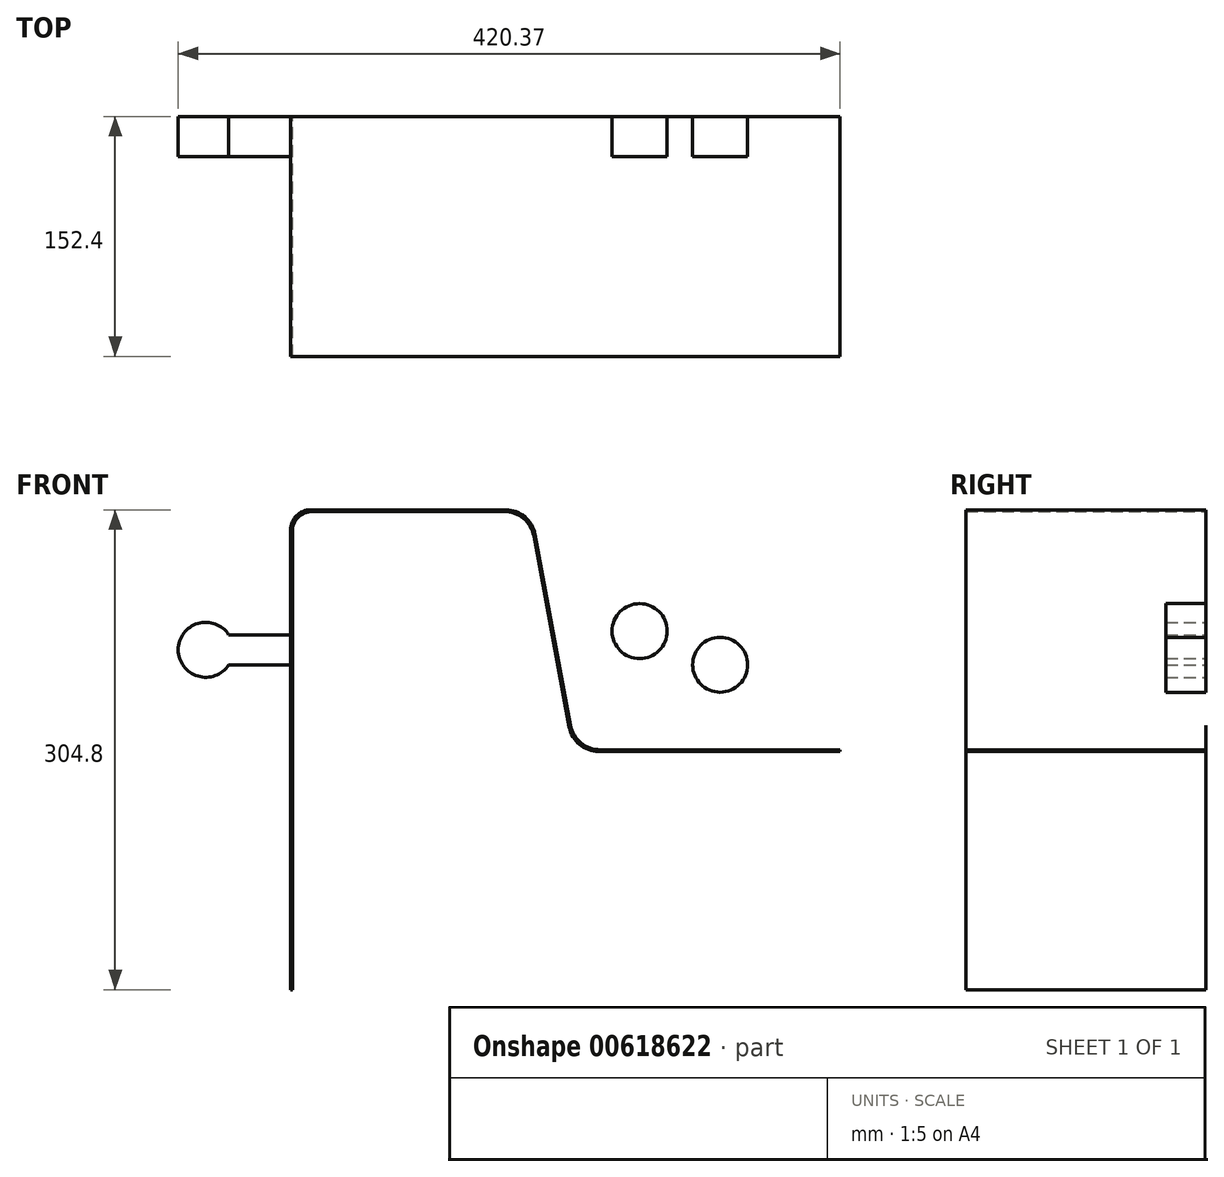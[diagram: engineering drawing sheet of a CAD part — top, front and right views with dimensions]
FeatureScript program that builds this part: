
annotation { "Feature Type Name" : "Feature", "Feature Type Description" : "" }
export const myFeature = defineFeature(function(context is Context, id is Id, definition is map)
    precondition{}
    {
        {
            var Q0;
            Q0=qCreatedBy(makeId("Front.planeOp"),FACE);
            var sketch = newSketch(context, id + "F0", { "sketchPlane" : qUnion([Q0])});
            skLineSegment(sketch, "E0", {"start": v(0, 0) * mm, "end": v(0, 292.1) * mm});
            skLineSegment(sketch, "E1", {"start": v(12.7, 304.8) * mm, "end": v(136.56, 304.8) * mm});
            skLineSegment(sketch, "E2", {"start": v(155.3, 289.23) * mm, "end": v(177.8, 167.97) * mm});
            skLineSegment(sketch, "E3", {"start": v(196.53, 152.4) * mm, "end": v(348.93, 152.4) * mm});
            skLineSegment(sketch, "E4.0", {"start": v(195.64, 151.33) * mm, "end": v(348.93, 151.33) * mm});
            skLineSegment(sketch, "E4.1", {"start": v(154.4, 288.16) * mm, "end": v(176.91, 166.9) * mm});
            skLineSegment(sketch, "E4.2", {"start": v(13.77, 303.73) * mm, "end": v(135.67, 303.73) * mm});
            skLineSegment(sketch, "E4.3", {"start": v(1.07, 0) * mm, "end": v(1.07, 291.03) * mm});
            skLineSegment(sketch, "E5", {"start": v(348.93, 151.33) * mm, "end": v(348.93, 152.4) * mm});
            skLineSegment(sketch, "E6", {"start": v(1.07, 0) * mm, "end": v(0, 0) * mm});
            skPoint(sketch, "E7.visualSharp", {"position": v(1.07, 303.73) * mm});
            skArc(sketch, "E7.filletArc", {"start": v(13.77, 303.73) * mm, "mid": v(4.79, 300.01) * mm, "end": v(1.07, 291.03) * mm});
            skPoint(sketch, "E8.visualSharp", {"position": v(0, 304.8) * mm});
            skArc(sketch, "E8.filletArc", {"start": v(12.7, 304.8) * mm, "mid": v(3.72, 301.08) * mm, "end": v(0, 292.1) * mm});
            skPoint(sketch, "E9.visualSharp", {"position": v(151.51, 303.73) * mm});
            skArc(sketch, "E9.filletArc", {"start": v(154.4, 288.16) * mm, "mid": v(147.85, 299.33) * mm, "end": v(135.67, 303.73) * mm});
            skPoint(sketch, "E10.visualSharp", {"position": v(152.4, 304.8) * mm});
            skArc(sketch, "E10.filletArc", {"start": v(155.3, 289.23) * mm, "mid": v(148.74, 300.4) * mm, "end": v(136.56, 304.8) * mm});
            skPoint(sketch, "E11.visualSharp", {"position": v(180.7, 152.4) * mm});
            skArc(sketch, "E11.filletArc", {"start": v(177.8, 167.97) * mm, "mid": v(184.35, 156.8) * mm, "end": v(196.53, 152.4) * mm});
            skPoint(sketch, "E12.visualSharp", {"position": v(179.8, 151.33) * mm});
            skArc(sketch, "E12.filletArc", {"start": v(176.91, 166.9) * mm, "mid": v(183.46, 155.74) * mm, "end": v(195.64, 151.33) * mm});
            skLineSegment(sketch, "E13.bottom", {"start": v(-39.34, 225.43) * mm, "end": v(0, 225.43) * mm});
            skLineSegment(sketch, "E13.top", {"start": v(-39.34, 206.38) * mm, "end": v(0, 206.38) * mm});
            skLineSegment(sketch, "E13.right", {"start": v(0, 225.43) * mm, "end": v(0, 206.38) * mm});
            skPoint(sketch, "E14", {"position": v(0, 215.9) * mm});
            skPoint(sketch, "E15", {"position": v(168.53, 217.92) * mm});
            skPoint(sketch, "E16", {"position": v(272.73, 152.4) * mm});
            skLineSegment(sketch, "E17", {"start": v(166.79, 227.28) * mm, "end": v(170.27, 208.55) * mm});
            skLineSegment(sketch, "E18", {"start": v(170.27, 208.55) * mm, "end": v(208.94, 215.73) * mm});
            skLineSegment(sketch, "E19", {"start": v(205.47, 234.46) * mm, "end": v(166.79, 227.28) * mm});
            skLineSegment(sketch, "E20.top", {"start": v(263.2, 152.4) * mm, "end": v(282.26, 152.4) * mm});
            skLineSegment(sketch, "E20.left", {"start": v(263.2, 191.74) * mm, "end": v(263.2, 152.4) * mm});
            skLineSegment(sketch, "E20.right", {"start": v(282.26, 191.74) * mm, "end": v(282.26, 152.4) * mm});
            skCircle(sketch, "E21", {"center": v(-53.98, 215.9) * mm, "radius": 17.46 * mm});
            skPoint(sketch, "E22", {"position": v(-63.5, 215.9) * mm});
            skPoint(sketch, "E23.orphan", {"position": v(-63.5, 225.43) * mm});
            skPoint(sketch, "E24.orphan", {"position": v(-63.5, 206.38) * mm});
            skCircle(sketch, "E25", {"center": v(221.6, 227.77) * mm, "radius": 17.46 * mm});
            skCircle(sketch, "E26", {"center": v(272.73, 206.38) * mm, "radius": 17.46 * mm});
            skPoint(sketch, "E27", {"position": v(230.96, 229.5) * mm});
            skPoint(sketch, "E28", {"position": v(272.73, 215.9) * mm});
            skPoint(sketch, "E29.orphan", {"position": v(232.7, 220.14) * mm});
            skPoint(sketch, "E30.end.orphan", {"position": v(229.22, 238.87) * mm});
            skPoint(sketch, "E31.orphan", {"position": v(263.2, 215.9) * mm});
            skPoint(sketch, "E32.orphan", {"position": v(282.26, 215.9) * mm});
            skSolve(sketch);
        }
        {
            var Q0;
            Q0=makeQuery(id+"F0.imprint","IMPRINT",FACE,{"disambiguationData":[TD([[makeQuery(id+"F0.imprint","IMPRINT",EDGE,{"derivedFrom":sQuery(id+"F0.wireOp",EDGE,"E1")}),-1.0]])]});
            extrude(context, id + "F1", {"entities" : qUnion([Q0]), "depth" : 152.4 * mm, "offsetDistance" : 25.4 * mm});
        }
        {
            var Q0;
            {var subQ0=sQuery(id+"F0.wireOp",EDGE,"E21");var subQ1=makeQuery(id+"F0.imprint","INTERSECT",VERTEX,{"derivedFrom":[sQuery(id+"F0.wireOp",EDGE,"E13.bottom"),subQ0]});Q0=makeQuery(id+"F0.imprint","IMPRINT",FACE,{"disambiguationData":[TD([[makeQuery(id+"F0.imprint","IMPRINT",EDGE,{"disambiguationData":[TD([[subQ1,-1.0]])],"derivedFrom":subQ0}),1.0]])]});}
            var Q1;
            {var subQ0=sQuery(id+"F0.wireOp",EDGE,"E13.bottom");Q1=makeQuery(id+"F0.imprint","IMPRINT",FACE,{"disambiguationData":[TD([[makeQuery(id+"F0.imprint","IMPRINT",EDGE,{"derivedFrom":subQ0}),-1.0]])]});}
            var Q2;
            Q2=makeQuery(id+"F0.imprint","IMPRINT",FACE,{"disambiguationData":[TD([[makeQuery(id+"F0.imprint","IMPRINT",EDGE,{"derivedFrom":sQuery(id+"F0.wireOp",EDGE,"E17")}),1.0]])]});
            var Q3;
            {var subQ0=sQuery(id+"F0.wireOp",EDGE,"E25");var subQ1=makeQuery(id+"F0.imprint","INTERSECT",VERTEX,{"derivedFrom":[sQuery(id+"F0.wireOp",EDGE,"E18"),subQ0]});Q3=makeQuery(id+"F0.imprint","IMPRINT",FACE,{"disambiguationData":[TD([[makeQuery(id+"F0.imprint","IMPRINT",EDGE,{"disambiguationData":[TD([[subQ1,1.0]])],"derivedFrom":subQ0}),1.0]])]});}
            var Q4;
            {var subQ0=sQuery(id+"F0.wireOp",EDGE,"E26");var subQ1=makeQuery(id+"F0.imprint","INTERSECT",VERTEX,{"derivedFrom":[sQuery(id+"F0.wireOp",EDGE,"E20.left"),subQ0]});Q4=makeQuery(id+"F0.imprint","IMPRINT",FACE,{"disambiguationData":[TD([[makeQuery(id+"F0.imprint","IMPRINT",EDGE,{"disambiguationData":[TD([[subQ1,-1.0]])],"derivedFrom":subQ0}),1.0]])]});}
            var Q5;
            Q5=makeQuery(id+"F0.imprint","IMPRINT",FACE,{"disambiguationData":[TD([[makeQuery(id+"F0.imprint","IMPRINT",EDGE,{"derivedFrom":sQuery(id+"F0.wireOp",EDGE,"E20.top")}),1.0]])]});
            extrude(context, id + "F2", {"entities" : qUnion([Q0, Q1, Q2, Q3, Q4, Q5]), "operationType" : NewBodyOperationType.ADD, "depth" : 25.4 * mm, "offsetDistance" : 25.4 * mm});
        }
    });
